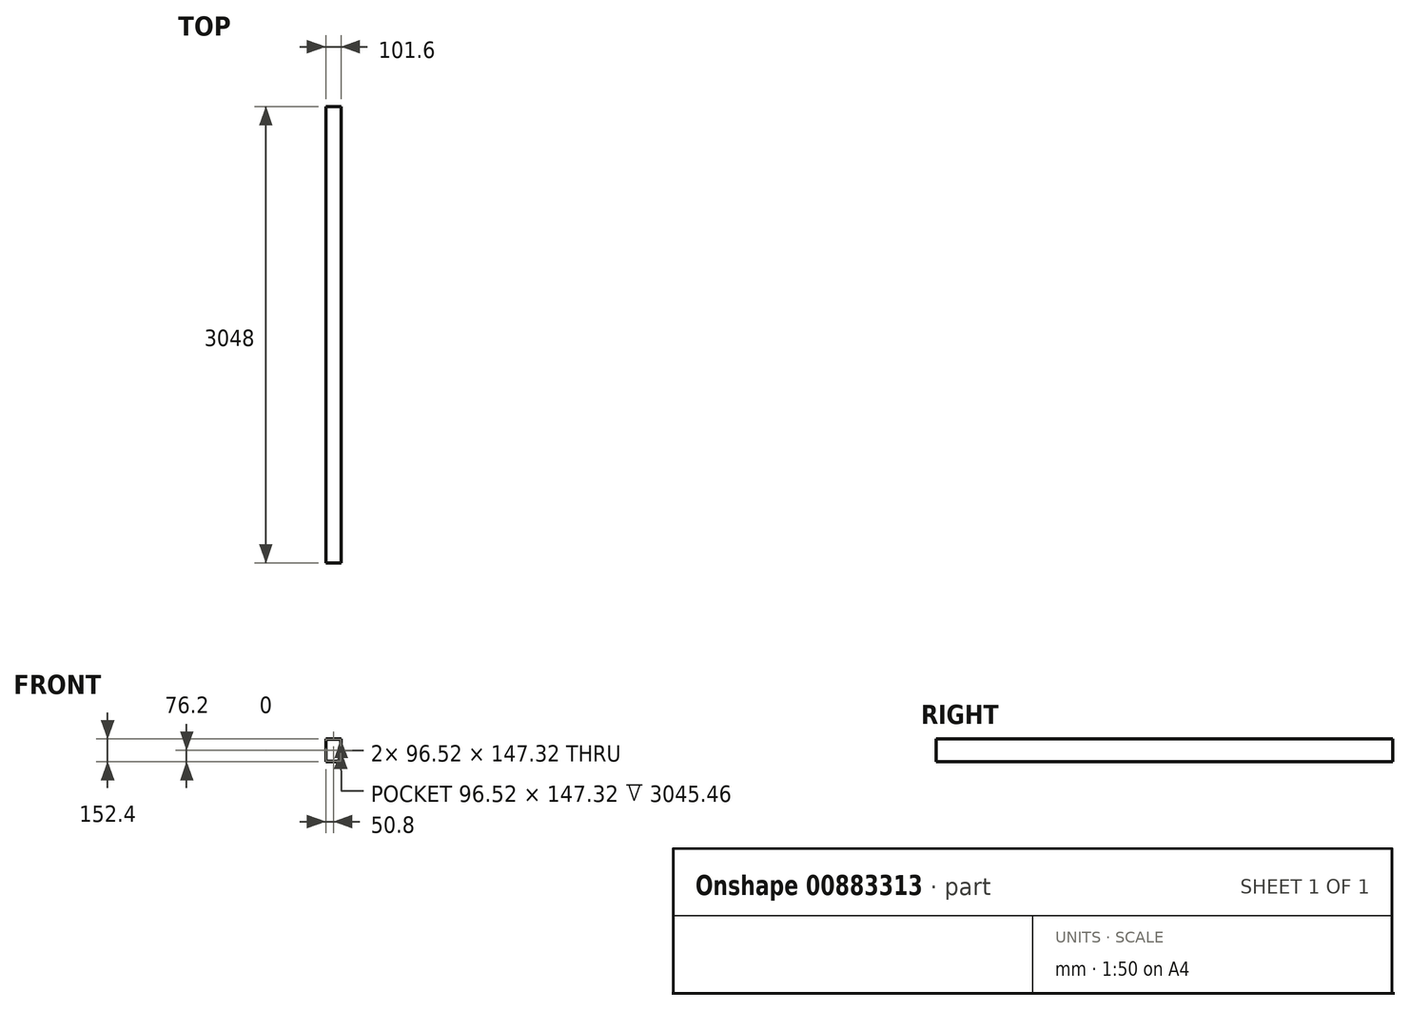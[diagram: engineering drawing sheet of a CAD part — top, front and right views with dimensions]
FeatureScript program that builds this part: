
annotation { "Feature Type Name" : "Feature", "Feature Type Description" : "" }
export const myFeature = defineFeature(function(context is Context, id is Id, definition is map)
    precondition{}
    {
        {
            var Q0;
            Q0=qCreatedBy(makeId("Front.planeOp"),FACE);
            var sketch = newSketch(context, id + "F0", { "sketchPlane" : qUnion([Q0])});
            skLineSegment(sketch, "E0.bottom", {"start": v(-50.8, -76.2) * mm, "end": v(50.8, -76.2) * mm});
            skLineSegment(sketch, "E0.top", {"start": v(-50.8, 76.2) * mm, "end": v(50.8, 76.2) * mm});
            skLineSegment(sketch, "E0.left", {"start": v(-50.8, -76.2) * mm, "end": v(-50.8, 76.2) * mm});
            skLineSegment(sketch, "E0.right", {"start": v(50.8, -76.2) * mm, "end": v(50.8, 76.2) * mm});
            skLineSegment(sketch, "E1", {"start": v(0, 76.2) * mm, "end": v(0, -76.2) * mm, "construction": true});
            skLineSegment(sketch, "E2", {"start": v(50.8, 0) * mm, "end": v(-50.8, 0) * mm, "construction": true});
            skPoint(sketch, "E3", {"position": v(0, 0) * mm});
            skSolve(sketch);
        }
        {
            var Q0;
            Q0=makeQuery(id+"F0.imprint","IMPRINT",FACE,{"disambiguationData":[TD([[makeQuery(id+"F0.imprint","IMPRINT",EDGE,{"derivedFrom":sQuery(id+"F0.wireOp",EDGE,"E0.bottom")}),1.0]])]});
            var Q1;
            Q1=sQuery(id+"F0.wireOp",EDGE,"E0.top");
            var Q2;
            Q2=sQuery(id+"F0.wireOp",EDGE,"E0.right");
            var Q3;
            Q3=sQuery(id+"F0.wireOp",EDGE,"E0.left");
            var Q4;
            Q4=sQuery(id+"F0.wireOp",EDGE,"E0.bottom");
            extrude(context, id + "F1", {"entities" : qUnion([Q0]), "surfaceEntities" : qUnion([Q1, Q2, Q3, Q4]), "endBound" : BoundingType.SYMMETRIC, "depth" : 3048 * mm, "offsetDistance" : 25.4 * mm});
        }
        {
            var Q0;
            Q0=makeQuery(id+"F1.opExtrude","CAP_FACE",FACE,{"disambiguationData":[OSD([sQuery(id+"F0.wireOp",EDGE,"E0.bottom"),sQuery(id+"F0.wireOp",EDGE,"E0.top"),sQuery(id+"F0.wireOp",EDGE,"E0.left"),sQuery(id+"F0.wireOp",EDGE,"E0.right")])],"isStart":false});
            shell(context, id + "F2", {"entities" : qUnion([Q0]), "thickness" : 2.54 * mm});
        }
    });
